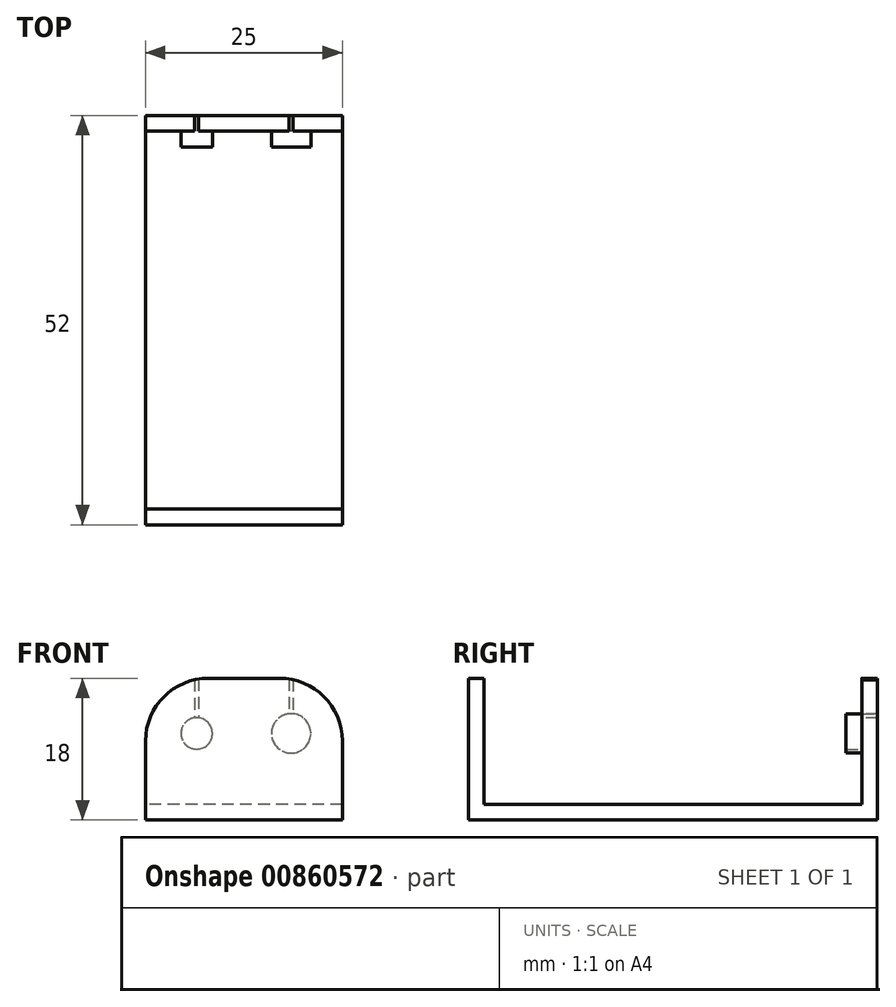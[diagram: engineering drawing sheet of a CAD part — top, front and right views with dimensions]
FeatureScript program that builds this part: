
annotation { "Feature Type Name" : "Feature", "Feature Type Description" : "" }
export const myFeature = defineFeature(function(context is Context, id is Id, definition is map)
    precondition{}
    {
        {
            var Q0;
            Q0=qCreatedBy(makeId("Top.planeOp"),FACE);
            var sketch = newSketch(context, id + "F0", { "sketchPlane" : qUnion([Q0])});
            skLineSegment(sketch, "E0.bottom", {"start": v(12.5, 26) * mm, "end": v(-12.5, 26) * mm});
            skLineSegment(sketch, "E0.top", {"start": v(12.5, -26) * mm, "end": v(-12.5, -26) * mm});
            skLineSegment(sketch, "E0.left", {"start": v(12.5, 26) * mm, "end": v(12.5, -26) * mm});
            skLineSegment(sketch, "E0.right", {"start": v(-12.5, 26) * mm, "end": v(-12.5, -26) * mm});
            skPoint(sketch, "E0.middle", {"position": v(0, 0) * mm});
            skSolve(sketch);
        }
        {
            var Q0;
            Q0=makeQuery(id+"F0.imprint","IMPRINT",FACE,{"disambiguationData":[TD([[makeQuery(id+"F0.imprint","IMPRINT",EDGE,{"derivedFrom":sQuery(id+"F0.wireOp",EDGE,"E0.bottom")}),1.0]])]});
            extrude(context, id + "F1", {"entities" : qUnion([Q0]), "depth" : 18 * mm, "offsetDistance" : 25 * mm});
        }
        {
            var Q0;
            Q0=makeQuery(id+"F1.opExtrude","CAP_FACE",FACE,{"disambiguationData":[OSD([sQuery(id+"F0.wireOp",EDGE,"E0.bottom"),sQuery(id+"F0.wireOp",EDGE,"E0.top"),sQuery(id+"F0.wireOp",EDGE,"E0.left"),sQuery(id+"F0.wireOp",EDGE,"E0.right")])],"isStart":false});
            var sketch = newSketch(context, id + "F2", { "sketchPlane" : qUnion([Q0])});
            skLineSegment(sketch, "E1.bottom", {"start": v(12.5, 24) * mm, "end": v(-12.5, 24) * mm});
            skLineSegment(sketch, "E1.top", {"start": v(12.5, -24) * mm, "end": v(-12.5, -24) * mm});
            skLineSegment(sketch, "E1.left", {"start": v(12.5, 24) * mm, "end": v(12.5, -24) * mm});
            skLineSegment(sketch, "E1.right", {"start": v(-12.5, 24) * mm, "end": v(-12.5, -24) * mm});
            skSolve(sketch);
        }
        {
            var Q0;
            Q0=makeQuery(id+"F2.imprint","IMPRINT",FACE,{"disambiguationData":[TD([[makeQuery(id+"F2.imprint","IMPRINT",EDGE,{"derivedFrom":sQuery(id+"F2.wireOp",EDGE,"E1.bottom")}),1.0]])]});
            extrude(context, id + "F3", {"entities" : qUnion([Q0]), "operationType" : NewBodyOperationType.REMOVE, "oppositeDirection" : true, "depth" : 16 * mm, "offsetDistance" : 25 * mm});
        }
        {
            var Q0;
            {var subQ0=sQuery(id+"F0.wireOp",EDGE,"E0.bottom");var subQ1=sQuery(id+"F0.wireOp",EDGE,"E0.right");Q0=makeQuery(id+"F3.boolean.opBoolean","SPLIT",EDGE,{"disambiguationData":[TD([makeQuery(id+"F1.opExtrude","SWEPT_FACE",FACE,{"disambiguationData":[OSD([subQ0])]})])],"derivedFrom":makeQuery(id+"F1.opExtrude","CAP_EDGE",EDGE,{"disambiguationData":[OSD([subQ1])],"isStart":false})});}
            var Q1;
            {var subQ0=sQuery(id+"F0.wireOp",EDGE,"E0.bottom");var subQ1=sQuery(id+"F0.wireOp",EDGE,"E0.left");Q1=makeQuery(id+"F3.boolean.opBoolean","SPLIT",EDGE,{"disambiguationData":[TD([makeQuery(id+"F1.opExtrude","SWEPT_FACE",FACE,{"disambiguationData":[OSD([subQ0])]})])],"derivedFrom":makeQuery(id+"F1.opExtrude","CAP_EDGE",EDGE,{"disambiguationData":[OSD([subQ1])],"isStart":false})});}
            var Q2;
            {var subQ0=sQuery(id+"F0.wireOp",EDGE,"E0.right");var subQ1=sQuery(id+"F0.wireOp",EDGE,"E0.top");Q2=makeQuery(id+"F3.boolean.opBoolean","SPLIT",EDGE,{"disambiguationData":[TD([makeQuery(id+"F1.opExtrude","SWEPT_FACE",FACE,{"disambiguationData":[OSD([subQ1])]})])],"derivedFrom":makeQuery(id+"F1.opExtrude","CAP_EDGE",EDGE,{"disambiguationData":[OSD([subQ0])],"isStart":false})});}
            var Q3;
            {var subQ0=sQuery(id+"F0.wireOp",EDGE,"E0.left");var subQ1=sQuery(id+"F0.wireOp",EDGE,"E0.top");Q3=makeQuery(id+"F3.boolean.opBoolean","SPLIT",EDGE,{"disambiguationData":[TD([makeQuery(id+"F1.opExtrude","SWEPT_FACE",FACE,{"disambiguationData":[OSD([subQ1])]})])],"derivedFrom":makeQuery(id+"F1.opExtrude","CAP_EDGE",EDGE,{"disambiguationData":[OSD([subQ0])],"isStart":false})});}
            fillet(context, id + "F4", {"entities" : qUnion([Q0, Q1, Q2, Q3]), "radius" : 7.97 * mm, "tangentPropagation" : true, "allowEdgeOverflow" : false});
        }
        {
            var Q0;
            Q0=makeQuery(id+"F3.boolean.opBoolean","COPY",FACE,{"derivedFrom":makeQuery(id+"F3.opExtrude","SWEPT_FACE",FACE,{"disambiguationData":[OSD([sQuery(id+"F2.wireOp",EDGE,"E1.bottom")])]})});
            var sketch = newSketch(context, id + "F5", { "sketchPlane" : qUnion([Q0])});
            skPoint(sketch, "E2", {"position": v(-6, 11) * mm});
            skPoint(sketch, "E3", {"position": v(6, 11) * mm});
            skCircle(sketch, "E4", {"center": v(6, 11) * mm, "radius": 2.5 * mm});
            skCircle(sketch, "E5", {"center": v(-6, 11) * mm, "radius": 2 * mm});
            skPoint(sketch, "E6", {"position": v(-6.25, 12.98) * mm});
            skPoint(sketch, "E7", {"position": v(-5.75, 12.98) * mm});
            skLineSegment(sketch, "E8", {"start": v(-6.25, 12.98) * mm, "end": v(-6.25, 17.81) * mm});
            skLineSegment(sketch, "E9", {"start": v(-5.75, 12.98) * mm, "end": v(-5.75, 17.9) * mm});
            skPoint(sketch, "E10", {"position": v(5.75, 13.49) * mm});
            skPoint(sketch, "E11", {"position": v(6.25, 13.49) * mm});
            skLineSegment(sketch, "E12", {"start": v(5.75, 13.49) * mm, "end": v(5.75, 17.9) * mm});
            skLineSegment(sketch, "E13", {"start": v(6.25, 13.49) * mm, "end": v(6.25, 17.81) * mm});
            skSolve(sketch);
        }
        {
            var Q0;
            Q0=makeQuery(id+"F5.imprint","IMPRINT",FACE,{"disambiguationData":[TD([[makeQuery(id+"F5.imprint","IMPRINT",EDGE,{"derivedFrom":sQuery(id+"F5.wireOp",EDGE,"E5")}),1.0]])]});
            var Q1;
            Q1=makeQuery(id+"F5.imprint","IMPRINT",FACE,{"disambiguationData":[TD([[makeQuery(id+"F5.imprint","IMPRINT",EDGE,{"derivedFrom":sQuery(id+"F5.wireOp",EDGE,"E4")}),1.0]])]});
            extrude(context, id + "F6", {"entities" : qUnion([Q0, Q1]), "operationType" : NewBodyOperationType.ADD, "depth" : 2 * mm, "offsetDistance" : 25 * mm});
        }
        {
            var Q0;
            {var subQ0=sQuery(id+"F5.wireOp",EDGE,"E8");Q0=makeQuery(id+"F5.imprint","IMPRINT",FACE,{"disambiguationData":[TD([[makeQuery(id+"F5.imprint","IMPRINT",EDGE,{"derivedFrom":subQ0}),-1.0]])]});}
            var Q1;
            {var subQ0=sQuery(id+"F5.wireOp",EDGE,"E12");Q1=makeQuery(id+"F5.imprint","IMPRINT",FACE,{"disambiguationData":[TD([[makeQuery(id+"F5.imprint","IMPRINT",EDGE,{"derivedFrom":subQ0}),-1.0]])]});}
            extrude(context, id + "F7", {"entities" : qUnion([Q0, Q1]), "operationType" : NewBodyOperationType.REMOVE, "endBound" : BoundingType.UP_TO_NEXT, "oppositeDirection" : true, "depth" : 25 * mm, "offsetDistance" : 25 * mm});
        }
    });
